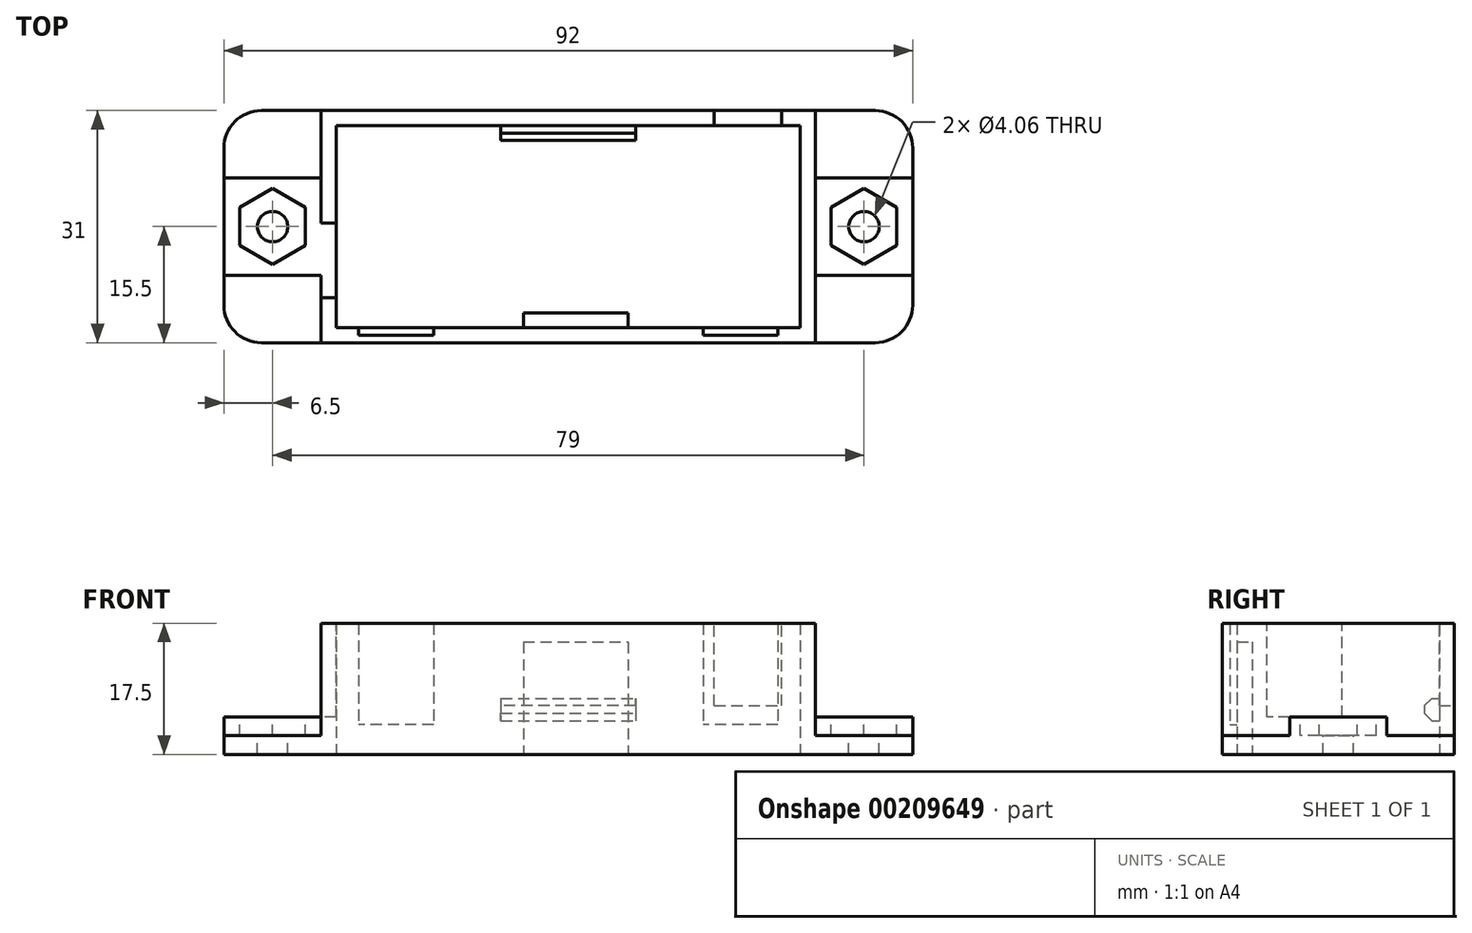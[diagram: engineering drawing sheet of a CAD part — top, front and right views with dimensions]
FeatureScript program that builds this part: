
annotation { "Feature Type Name" : "Feature", "Feature Type Description" : "" }
export const myFeature = defineFeature(function(context is Context, id is Id, definition is map)
    precondition{}
    {
        {
            var Q0;
            Q0=qCreatedBy(makeId("Top.planeOp"),FACE);
            var sketch = newSketch(context, id + "F0", { "sketchPlane" : qUnion([Q0])});
            skLineSegment(sketch, "E0.bottom", {"start": v(0, 0) * mm, "end": v(92, 0) * mm});
            skLineSegment(sketch, "E0.top", {"start": v(0, 31) * mm, "end": v(92, 31) * mm});
            skLineSegment(sketch, "E0.left", {"start": v(0, 0) * mm, "end": v(0, 31) * mm});
            skLineSegment(sketch, "E0.right", {"start": v(92, 0) * mm, "end": v(92, 31) * mm});
            skSolve(sketch);
        }
        {
            var Q0;
            Q0=makeQuery(id+"F0.imprint","IMPRINT",FACE,{"disambiguationData":[TD([[makeQuery(id+"F0.imprint","IMPRINT",EDGE,{"derivedFrom":sQuery(id+"F0.wireOp",EDGE,"E0.bottom")}),1.0]])]});
            extrude(context, id + "F1", {"entities" : qUnion([Q0]), "depth" : 2.5 * mm});
        }
        {
            var Q0;
            Q0=makeQuery(id+"F1.opExtrude","CAP_FACE",FACE,{"disambiguationData":[OSD([sQuery(id+"F0.wireOp",EDGE,"E0.bottom"),sQuery(id+"F0.wireOp",EDGE,"E0.top"),sQuery(id+"F0.wireOp",EDGE,"E0.left"),sQuery(id+"F0.wireOp",EDGE,"E0.right")])],"isStart":false});
            var sketch = newSketch(context, id + "F2", { "sketchPlane" : qUnion([Q0])});
            skLineSegment(sketch, "E1", {"start": v(13, 31) * mm, "end": v(13, 0) * mm});
            skLineSegment(sketch, "E2", {"start": v(79, 31) * mm, "end": v(79, 0) * mm});
            skLineSegment(sketch, "E3.bottom", {"start": v(15, 29) * mm, "end": v(77, 29) * mm});
            skLineSegment(sketch, "E3.top", {"start": v(15, 2) * mm, "end": v(77, 2) * mm});
            skLineSegment(sketch, "E3.left", {"start": v(15, 29) * mm, "end": v(15, 2) * mm});
            skLineSegment(sketch, "E3.right", {"start": v(77, 29) * mm, "end": v(77, 2) * mm});
            skSolve(sketch);
        }
        {
            var Q0;
            {var subQ1=sQuery(id+"F2.wireOp",EDGE,"E1");Q0=makeQuery(id+"F2.imprint","IMPRINT",FACE,{"disambiguationData":[TD([[makeQuery(id+"F2.imprint","IMPRINT",EDGE,{"derivedFrom":subQ1}),1.0]])]});}
            extrude(context, id + "F3", {"entities" : qUnion([Q0]), "operationType" : NewBodyOperationType.ADD, "depth" : 15 * mm});
        }
        {
            var Q0;
            Q0=makeQuery(id+"F3.boolean.opBoolean","SPLIT",FACE,{"disambiguationData":[TD([makeQuery(id+"F3.opExtrude","SWEPT_FACE",FACE,{"disambiguationData":[OSD([sQuery(id+"F2.wireOp",EDGE,"E3.bottom")])]})])],"derivedFrom":makeQuery(id+"F1.opExtrude","CAP_FACE",FACE,{"disambiguationData":[OSD([sQuery(id+"F0.wireOp",EDGE,"E0.bottom"),sQuery(id+"F0.wireOp",EDGE,"E0.top"),sQuery(id+"F0.wireOp",EDGE,"E0.left"),sQuery(id+"F0.wireOp",EDGE,"E0.right")])],"isStart":false})});
            extrude(context, id + "F4", {"entities" : qUnion([Q0]), "operationType" : NewBodyOperationType.REMOVE, "oppositeDirection" : true, "depth" : 25 * mm});
        }
        {
            var Q0;
            {var subQ0=sQuery(id+"F0.wireOp",EDGE,"E0.left");var subQ1=sQuery(id+"F0.wireOp",EDGE,"E0.top");var subQ2=sQuery(id+"F0.wireOp",EDGE,"E0.bottom");Q0=makeQuery(id+"F3.boolean.opBoolean","SPLIT",FACE,{"disambiguationData":[TD([makeQuery(id+"F1.opExtrude","SWEPT_FACE",FACE,{"disambiguationData":[OSD([subQ0])]})])],"derivedFrom":makeQuery(id+"F1.opExtrude","CAP_FACE",FACE,{"disambiguationData":[OSD([subQ2,subQ1,subQ0,sQuery(id+"F0.wireOp",EDGE,"E0.right")])],"isStart":false})});}
            var sketch = newSketch(context, id + "F5", { "sketchPlane" : qUnion([Q0])});
            skLineSegment(sketch, "E4.bottom", {"start": v(13, 22) * mm, "end": v(0, 22) * mm});
            skLineSegment(sketch, "E4.top", {"start": v(13, 9) * mm, "end": v(0, 9) * mm});
            skLineSegment(sketch, "E4.left", {"start": v(13, 22) * mm, "end": v(13, 9) * mm});
            skLineSegment(sketch, "E4.right", {"start": v(0, 22) * mm, "end": v(0, 9) * mm});
            skLineSegment(sketch, "E5.bottom", {"start": v(92, 22) * mm, "end": v(79, 22) * mm});
            skLineSegment(sketch, "E5.top", {"start": v(92, 9) * mm, "end": v(79, 9) * mm});
            skLineSegment(sketch, "E5.left", {"start": v(92, 22) * mm, "end": v(92, 9) * mm});
            skLineSegment(sketch, "E5.right", {"start": v(79, 22) * mm, "end": v(79, 9) * mm});
            skSolve(sketch);
        }
        {
            var Q0;
            Q0=makeQuery(id+"F5.imprint","IMPRINT",FACE,{"disambiguationData":[TD([[makeQuery(id+"F5.imprint","IMPRINT",EDGE,{"derivedFrom":sQuery(id+"F5.wireOp",EDGE,"E5.bottom")}),1.0]])]});
            var Q1;
            Q1=makeQuery(id+"F5.imprint","IMPRINT",FACE,{"disambiguationData":[TD([[makeQuery(id+"F5.imprint","IMPRINT",EDGE,{"derivedFrom":sQuery(id+"F5.wireOp",EDGE,"E4.bottom")}),1.0]])]});
            extrude(context, id + "F6", {"entities" : qUnion([Q0, Q1]), "operationType" : NewBodyOperationType.ADD, "depth" : 2.5 * mm});
        }
        {
            var Q0;
            Q0=makeQuery(id+"F6.opExtrude","CAP_FACE",FACE,{"disambiguationData":[OSD([sQuery(id+"F5.wireOp",EDGE,"E4.bottom"),sQuery(id+"F5.wireOp",EDGE,"E4.top"),sQuery(id+"F5.wireOp",EDGE,"E4.left"),sQuery(id+"F5.wireOp",EDGE,"E4.right")])],"isStart":false});
            var sketch = newSketch(context, id + "F7", { "sketchPlane" : qUnion([Q0])});
            skCircle(sketch, "E6", {"center": v(6.5, 15.5) * mm, "radius": 2.03 * mm});
            skPoint(sketch, "E6.centerSnap0", {"position": v(6.5, 9) * mm});
            skPoint(sketch, "E6.centerSnap1", {"position": v(13, 15.5) * mm});
            skCircle(sketch, "E7", {"center": v(85.5, 15.5) * mm, "radius": 2.03 * mm});
            skSolve(sketch);
        }
        {
            var Q0;
            Q0=makeQuery(id+"F7.imprint","IMPRINT",FACE,{"disambiguationData":[TD([[makeQuery(id+"F7.imprint","IMPRINT",EDGE,{"derivedFrom":sQuery(id+"F7.wireOp",EDGE,"E7")}),1.0]])]});
            var Q1;
            Q1=makeQuery(id+"F7.imprint","IMPRINT",FACE,{"disambiguationData":[TD([[makeQuery(id+"F7.imprint","IMPRINT",EDGE,{"derivedFrom":sQuery(id+"F7.wireOp",EDGE,"E6")}),1.0]])]});
            extrude(context, id + "F8", {"entities" : qUnion([Q0, Q1]), "operationType" : NewBodyOperationType.REMOVE, "endBound" : BoundingType.THROUGH_ALL, "oppositeDirection" : true, "depth" : 25 * mm});
        }
        {
            var Q0;
            Q0=makeQuery(id+"F6.opExtrude","CAP_FACE",FACE,{"disambiguationData":[OSD([sQuery(id+"F5.wireOp",EDGE,"E4.bottom"),sQuery(id+"F5.wireOp",EDGE,"E4.top"),sQuery(id+"F5.wireOp",EDGE,"E4.left"),sQuery(id+"F5.wireOp",EDGE,"E4.right")])],"isStart":false});
            var sketch = newSketch(context, id + "F9", { "sketchPlane" : qUnion([Q0])});
            skCircle(sketch, "E8.cCircle", {"center": v(6.5, 15.5) * mm, "radius": 4.4 * mm, "construction": true});
            skLineSegment(sketch, "E8.0", {"start": v(2.1, 12.96) * mm, "end": v(2.1, 18.04) * mm});
            skLineSegment(sketch, "E8.1", {"start": v(2.1, 18.04) * mm, "end": v(6.5, 20.58) * mm});
            skLineSegment(sketch, "E8.2", {"start": v(6.5, 20.58) * mm, "end": v(10.9, 18.04) * mm});
            skLineSegment(sketch, "E8.3", {"start": v(10.9, 18.04) * mm, "end": v(10.9, 12.96) * mm});
            skLineSegment(sketch, "E8.4", {"start": v(10.9, 12.96) * mm, "end": v(6.5, 10.42) * mm});
            skLineSegment(sketch, "E8.5", {"start": v(6.5, 10.42) * mm, "end": v(2.1, 12.96) * mm});
            skPoint(sketch, "E8.0.midPoint", {"position": v(2.1, 15.5) * mm});
            skCircle(sketch, "E9.cCircle", {"center": v(85.5, 15.5) * mm, "radius": 4.4 * mm, "construction": true});
            skLineSegment(sketch, "E9.0", {"start": v(85.5, 10.42) * mm, "end": v(81.1, 12.96) * mm});
            skLineSegment(sketch, "E9.1", {"start": v(81.1, 12.96) * mm, "end": v(81.1, 18.04) * mm});
            skLineSegment(sketch, "E9.2", {"start": v(81.1, 18.04) * mm, "end": v(85.5, 20.58) * mm});
            skLineSegment(sketch, "E9.3", {"start": v(85.5, 20.58) * mm, "end": v(89.9, 18.04) * mm});
            skLineSegment(sketch, "E9.4", {"start": v(89.9, 18.04) * mm, "end": v(89.9, 12.96) * mm});
            skLineSegment(sketch, "E9.5", {"start": v(89.9, 12.96) * mm, "end": v(85.5, 10.42) * mm});
            skPoint(sketch, "E9.0.midPoint", {"position": v(83.3, 11.69) * mm});
            skSolve(sketch);
        }
        {
            var Q0;
            Q0=makeQuery(id+"F9.imprint","IMPRINT",FACE,{"disambiguationData":[TD([[makeQuery(id+"F9.imprint","IMPRINT",EDGE,{"derivedFrom":sQuery(id+"F9.wireOp",EDGE,"E8.0")}),-1.0]])]});
            var Q1;
            Q1=makeQuery(id+"F9.imprint","IMPRINT",FACE,{"disambiguationData":[TD([[makeQuery(id+"F9.imprint","IMPRINT",EDGE,{"derivedFrom":sQuery(id+"F9.wireOp",EDGE,"E9.0")}),-1.0]])]});
            var Q2;
            {var subQ1=sQuery(id+"F0.wireOp",EDGE,"E0.left");var subQ2=makeQuery(id+"F1.opExtrude","SWEPT_FACE",FACE,{"disambiguationData":[OSD([subQ1])]});var subQ4=sQuery(id+"F0.wireOp",EDGE,"E0.bottom");var subQ5=makeQuery(id+"F1.opExtrude","SWEPT_FACE",FACE,{"disambiguationData":[OSD([subQ4])]});var subQ6=sQuery(id+"F0.wireOp",EDGE,"E0.top");Q2=makeQuery(id+"F6.boolean.opBoolean","SPLIT",FACE,{"disambiguationData":[TD([subQ5])],"derivedFrom":makeQuery(id+"F3.boolean.opBoolean","SPLIT",FACE,{"disambiguationData":[TD([subQ2])],"derivedFrom":makeQuery(id+"F1.opExtrude","CAP_FACE",FACE,{"disambiguationData":[OSD([subQ4,subQ6,subQ1,sQuery(id+"F0.wireOp",EDGE,"E0.right")])],"isStart":false})})});}
            extrude(context, id + "F10", {"entities" : qUnion([Q0, Q1]), "operationType" : NewBodyOperationType.REMOVE, "endBound" : BoundingType.UP_TO_SURFACE, "oppositeDirection" : true, "endBoundEntityFace" : qUnion([Q2]), "depth" : 25 * mm});
        }
        {
            var Q0;
            Q0=qCreatedBy(makeId("Top.planeOp"),FACE);
            var sketch = newSketch(context, id + "F11", { "sketchPlane" : qUnion([Q0])});
            skLineSegment(sketch, "E10.bottom", {"start": v(40, 2) * mm, "end": v(54, 2) * mm});
            skLineSegment(sketch, "E10.top", {"start": v(40, 4) * mm, "end": v(54, 4) * mm});
            skLineSegment(sketch, "E10.left", {"start": v(40, 2) * mm, "end": v(40, 4) * mm});
            skLineSegment(sketch, "E10.right", {"start": v(54, 2) * mm, "end": v(54, 4) * mm});
            skSolve(sketch);
        }
        {
            var Q0;
            Q0=makeQuery(id+"F11.imprint","IMPRINT",FACE,{"disambiguationData":[TD([[makeQuery(id+"F11.imprint","IMPRINT",EDGE,{"derivedFrom":sQuery(id+"F11.wireOp",EDGE,"E10.bottom")}),1.0]])]});
            extrude(context, id + "F12", {"entities" : qUnion([Q0]), "operationType" : NewBodyOperationType.ADD, "depth" : 15 * mm});
        }
        {
            var Q0;
            Q0=makeQuery(id+"F3.opExtrude","SWEPT_FACE",FACE,{"disambiguationData":[OSD([sQuery(id+"F2.wireOp",EDGE,"E1")])]});
            var sketch = newSketch(context, id + "F13", { "sketchPlane" : qUnion([Q0])});
            skLineSegment(sketch, "E11.bottom", {"start": v(-16, 5) * mm, "end": v(-6, 5) * mm});
            skLineSegment(sketch, "E11.top", {"start": v(-16, 17.5) * mm, "end": v(-6, 17.5) * mm});
            skLineSegment(sketch, "E11.left", {"start": v(-16, 5) * mm, "end": v(-16, 17.5) * mm});
            skLineSegment(sketch, "E11.right", {"start": v(-6, 5) * mm, "end": v(-6, 17.5) * mm});
            skSolve(sketch);
        }
        {
            var Q0;
            {var subQ1=sQuery(id+"F13.wireOp",EDGE,"E11.top");Q0=makeQuery(id+"F13.imprint","IMPRINT",FACE,{"disambiguationData":[TD([[makeQuery(id+"F13.imprint","IMPRINT",EDGE,{"derivedFrom":subQ1}),-1.0]])]});}
            extrude(context, id + "F14", {"entities" : qUnion([Q0]), "operationType" : NewBodyOperationType.REMOVE, "endBound" : BoundingType.UP_TO_NEXT, "oppositeDirection" : true, "depth" : 25 * mm});
        }
        {
            var Q0;
            {var subQ0=sQuery(id+"F2.wireOp",EDGE,"E3.bottom");Q0=makeQuery(id+"F4.boolean.opBoolean","MERGE",FACE,{"derivedFrom":[makeQuery(id+"F3.opExtrude","SWEPT_FACE",FACE,{"disambiguationData":[OSD([subQ0])]}),makeQuery(id+"F4.opExtrude","SWEPT_FACE",FACE,{"disambiguationData":[OSD([subQ0])]})]});}
            var sketch = newSketch(context, id + "F15", { "sketchPlane" : qUnion([Q0])});
            skLineSegment(sketch, "E12.bottom", {"start": v(37, 7.5) * mm, "end": v(55, 7.5) * mm});
            skLineSegment(sketch, "E12.top", {"start": v(37, 4.5) * mm, "end": v(55, 4.5) * mm});
            skLineSegment(sketch, "E12.left", {"start": v(37, 7.5) * mm, "end": v(37, 4.5) * mm});
            skLineSegment(sketch, "E12.right", {"start": v(55, 7.5) * mm, "end": v(55, 4.5) * mm});
            skSolve(sketch);
        }
        {
            var Q0;
            Q0=makeQuery(id+"F15.imprint","IMPRINT",FACE,{"disambiguationData":[TD([[makeQuery(id+"F15.imprint","IMPRINT",EDGE,{"derivedFrom":sQuery(id+"F15.wireOp",EDGE,"E12.bottom")}),-1.0]])]});
            extrude(context, id + "F16", {"entities" : qUnion([Q0]), "operationType" : NewBodyOperationType.ADD, "depth" : 2 * mm});
        }
        {
            var Q0;
            Q0=makeQuery(id+"F16.opExtrude","CAP_EDGE",EDGE,{"disambiguationData":[OSD([sQuery(id+"F15.wireOp",EDGE,"E12.bottom")])],"isStart":false});
            var Q1;
            Q1=makeQuery(id+"F16.opExtrude","CAP_EDGE",EDGE,{"disambiguationData":[OSD([sQuery(id+"F15.wireOp",EDGE,"E12.top")])],"isStart":false});
            chamfer(context, id + "F17", {"entities" : qUnion([Q0, Q1]), "width" : 1 * mm, "tangentPropagation" : true});
        }
        {
            var Q0;
            Q0=makeQuery(id+"F1.opExtrude","SWEPT_EDGE",EDGE,{"disambiguationData":[OSD([sQuery(id+"F0.wireOp",EDGE,"E0.bottom"),sQuery(id+"F0.wireOp",EDGE,"E0.left")])]});
            var Q1;
            Q1=makeQuery(id+"F1.opExtrude","SWEPT_EDGE",EDGE,{"disambiguationData":[OSD([sQuery(id+"F0.wireOp",EDGE,"E0.top"),sQuery(id+"F0.wireOp",EDGE,"E0.left")])]});
            var Q2;
            Q2=makeQuery(id+"F1.opExtrude","SWEPT_EDGE",EDGE,{"disambiguationData":[OSD([sQuery(id+"F0.wireOp",EDGE,"E0.bottom"),sQuery(id+"F0.wireOp",EDGE,"E0.right")])]});
            var Q3;
            Q3=makeQuery(id+"F1.opExtrude","SWEPT_EDGE",EDGE,{"disambiguationData":[OSD([sQuery(id+"F0.wireOp",EDGE,"E0.top"),sQuery(id+"F0.wireOp",EDGE,"E0.right")])]});
            fillet(context, id + "F18", {"entities" : qUnion([Q0, Q1, Q2, Q3]), "radius" : 5 * mm, "tangentPropagation" : true, "allowEdgeOverflow" : false});
        }
        {
            var Q0;
            {var subQ0=sQuery(id+"F2.wireOp",EDGE,"E3.top");Q0=makeQuery(id+"F4.boolean.opBoolean","MERGE",FACE,{"derivedFrom":[makeQuery(id+"F3.opExtrude","SWEPT_FACE",FACE,{"disambiguationData":[OSD([subQ0])]}),makeQuery(id+"F4.opExtrude","SWEPT_FACE",FACE,{"disambiguationData":[OSD([subQ0])]})]});}
            var sketch = newSketch(context, id + "F19", { "sketchPlane" : qUnion([Q0])});
            skLineSegment(sketch, "E13.bottom", {"start": v(-74, 17.5) * mm, "end": v(-64, 17.5) * mm});
            skLineSegment(sketch, "E13.top", {"start": v(-74, 4) * mm, "end": v(-64, 4) * mm});
            skLineSegment(sketch, "E13.left", {"start": v(-74, 17.5) * mm, "end": v(-74, 4) * mm});
            skLineSegment(sketch, "E13.right", {"start": v(-64, 17.5) * mm, "end": v(-64, 4) * mm});
            skLineSegment(sketch, "E14.bottom", {"start": v(-28, 17.5) * mm, "end": v(-18, 17.5) * mm});
            skLineSegment(sketch, "E14.top", {"start": v(-28, 4) * mm, "end": v(-18, 4) * mm});
            skLineSegment(sketch, "E14.left", {"start": v(-28, 17.5) * mm, "end": v(-28, 4) * mm});
            skLineSegment(sketch, "E14.right", {"start": v(-18, 17.5) * mm, "end": v(-18, 4) * mm});
            skSolve(sketch);
        }
        {
            var Q0;
            Q0=makeQuery(id+"F19.imprint","IMPRINT",FACE,{"disambiguationData":[TD([[makeQuery(id+"F19.imprint","IMPRINT",EDGE,{"derivedFrom":sQuery(id+"F19.wireOp",EDGE,"E13.bottom")}),1.0]])]});
            var Q1;
            Q1=makeQuery(id+"F19.imprint","IMPRINT",FACE,{"disambiguationData":[TD([[makeQuery(id+"F19.imprint","IMPRINT",EDGE,{"derivedFrom":sQuery(id+"F19.wireOp",EDGE,"E14.bottom")}),1.0]])]});
            extrude(context, id + "F20", {"entities" : qUnion([Q0, Q1]), "operationType" : NewBodyOperationType.REMOVE, "oppositeDirection" : true, "depth" : 1 * mm});
        }
        {
            var Q0;
            {var subQ0=sQuery(id+"F0.wireOp",EDGE,"E0.top");Q0=makeQuery(id+"F3.boolean.opBoolean","MERGE",FACE,{"derivedFrom":[makeQuery(id+"F1.opExtrude","SWEPT_FACE",FACE,{"disambiguationData":[OSD([subQ0])]}),makeQuery(id+"F3.opExtrude","SWEPT_FACE",FACE,{"disambiguationData":[OSD([subQ0])]})]});}
            var sketch = newSketch(context, id + "F21", { "sketchPlane" : qUnion([Q0])});
            skLineSegment(sketch, "E15.bottom", {"start": v(-74.5, 17.5) * mm, "end": v(-65.5, 17.5) * mm});
            skLineSegment(sketch, "E15.top", {"start": v(-74.5, 6.5) * mm, "end": v(-65.5, 6.5) * mm});
            skLineSegment(sketch, "E15.left", {"start": v(-74.5, 17.5) * mm, "end": v(-74.5, 6.5) * mm});
            skLineSegment(sketch, "E15.right", {"start": v(-65.5, 17.5) * mm, "end": v(-65.5, 6.5) * mm});
            skSolve(sketch);
        }
        {
            var Q0;
            Q0=makeQuery(id+"F21.imprint","IMPRINT",FACE,{"disambiguationData":[TD([[makeQuery(id+"F21.imprint","IMPRINT",EDGE,{"derivedFrom":sQuery(id+"F21.wireOp",EDGE,"E15.bottom")}),1.0]])]});
            extrude(context, id + "F22", {"entities" : qUnion([Q0]), "operationType" : NewBodyOperationType.REMOVE, "endBound" : BoundingType.UP_TO_NEXT, "oppositeDirection" : true, "depth" : 25 * mm});
        }
    });
